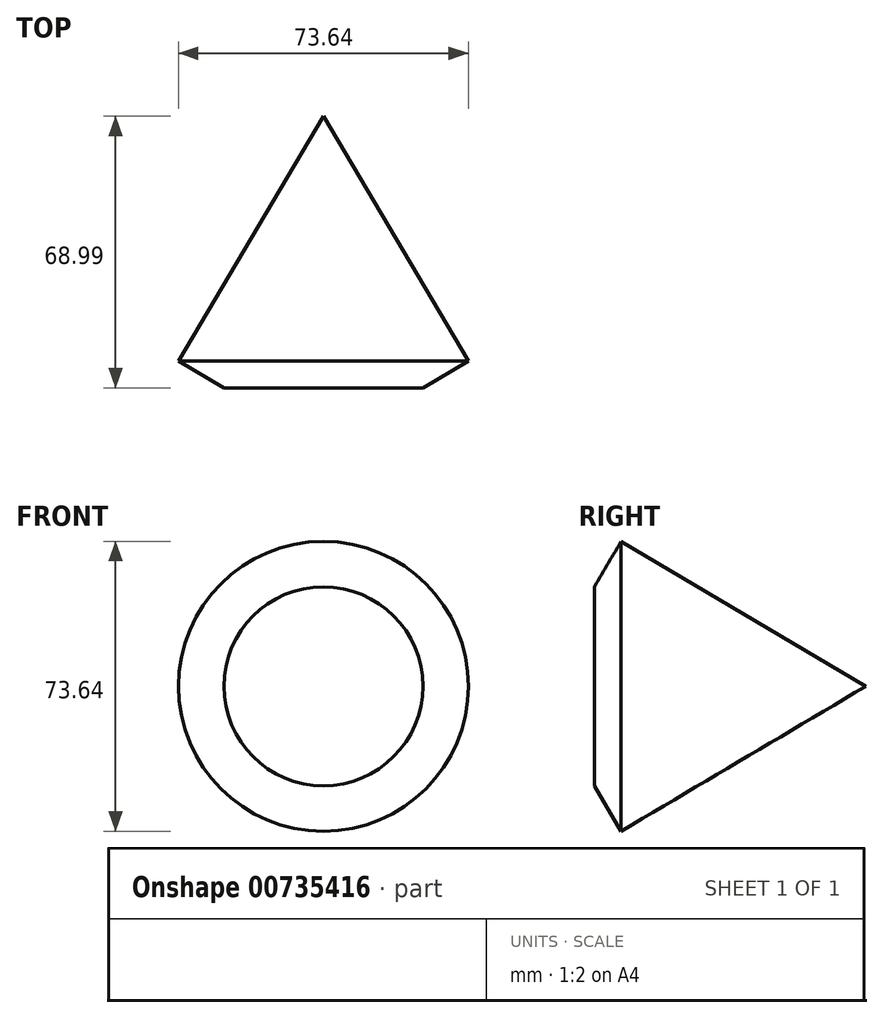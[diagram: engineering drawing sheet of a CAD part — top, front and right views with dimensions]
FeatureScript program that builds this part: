
annotation { "Feature Type Name" : "Feature", "Feature Type Description" : "" }
export const myFeature = defineFeature(function(context is Context, id is Id, definition is map)
    precondition{}
    {
        {
            var Q0;
            Q0=qCreatedBy(makeId("Top.planeOp"),FACE);
            var sketch = newSketch(context, id + "F0", { "sketchPlane" : qUnion([Q0])});
            skLineSegment(sketch, "E0", {"start": v(0, 0) * mm, "end": v(-36.82, -62.14) * mm});
            skLineSegment(sketch, "E1", {"start": v(-36.82, -62.14) * mm, "end": v(-25.27, -68.99) * mm});
            skLineSegment(sketch, "E2", {"start": v(-25.27, -68.99) * mm, "end": v(0, -68.99) * mm});
            skLineSegment(sketch, "E3", {"start": v(0, 0) * mm, "end": v(0, -68.99) * mm});
            skSolve(sketch);
        }
        {
            var Q0;
            Q0 = qSketchRegion(id + "F0", true);
            var Q1;
            Q1=sQuery(id+"F0.wireOp",EDGE,"E3");
            revolve(context, id + "F1", {"surfaceOperationType" : NewSurfaceOperationType.NEW, "entities" : qUnion([Q0]), "axis" : qUnion([Q1]), "revolveType" : RevolveType.FULL});
        }
    });
